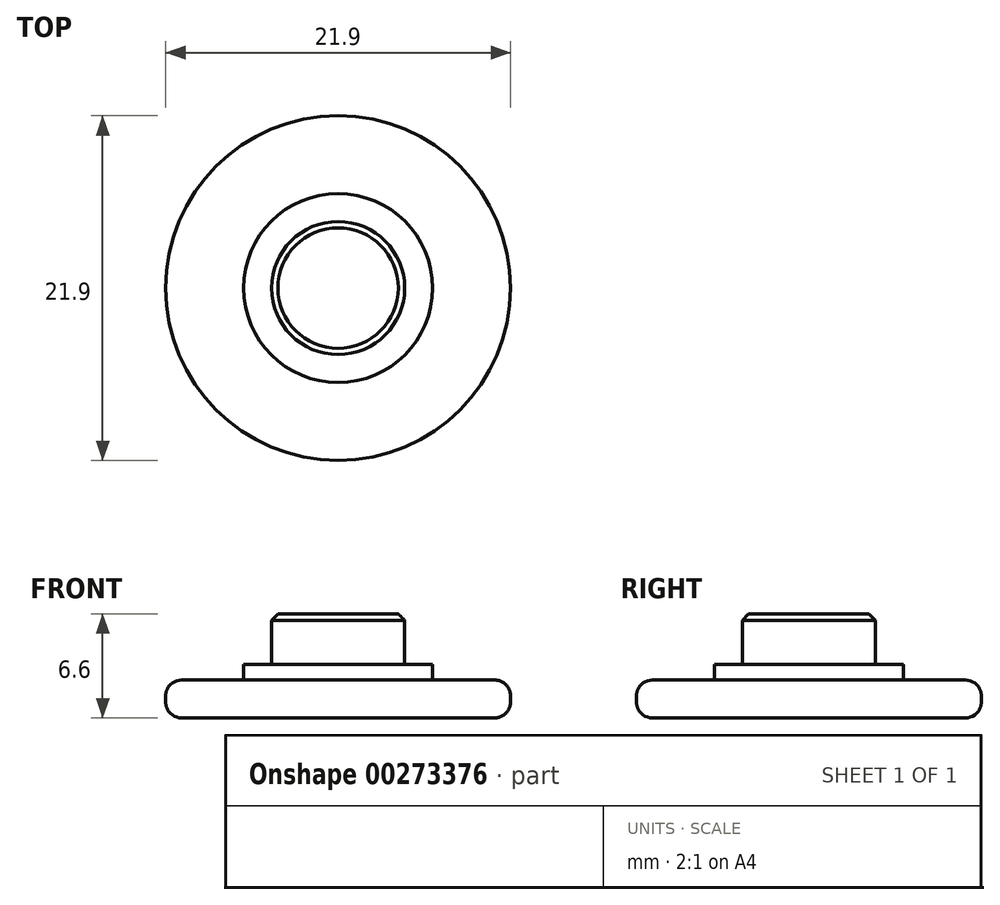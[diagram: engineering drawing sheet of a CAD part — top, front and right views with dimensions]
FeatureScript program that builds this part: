
annotation { "Feature Type Name" : "Feature", "Feature Type Description" : "" }
export const myFeature = defineFeature(function(context is Context, id is Id, definition is map)
    precondition{}
    {
        {
            var Q0;
            Q0=qCreatedBy(makeId("Top.planeOp"),FACE);
            var sketch = newSketch(context, id + "F0", { "sketchPlane" : qUnion([Q0])});
            skCircle(sketch, "E0", {"center": v(0, 0) * mm, "radius": 10.95 * mm});
            skSolve(sketch);
        }
        {
            var Q0;
            Q0=makeQuery(id+"F0.imprint","IMPRINT",FACE,{"disambiguationData":[TD([[makeQuery(id+"F0.imprint","IMPRINT",EDGE,{"derivedFrom":sQuery(id+"F0.wireOp",EDGE,"E0")}),1.0]])]});
            extrude(context, id + "F1", {"entities" : qUnion([Q0]), "depth" : 2.4 * mm});
        }
        {
            var Q0;
            Q0=makeQuery(id+"F1.opExtrude","CAP_FACE",FACE,{"disambiguationData":[OSD([sQuery(id+"F0.wireOp",EDGE,"E0")])],"isStart":false});
            var sketch = newSketch(context, id + "F2", { "sketchPlane" : qUnion([Q0])});
            skCircle(sketch, "E1", {"center": v(0, 0) * mm, "radius": 4.22 * mm});
            skSolve(sketch);
        }
        {
            var Q0;
            Q0=makeQuery(id+"F2.imprint","IMPRINT",FACE,{"disambiguationData":[TD([[makeQuery(id+"F2.imprint","IMPRINT",EDGE,{"derivedFrom":sQuery(id+"F2.wireOp",EDGE,"E1")}),1.0]])]});
            extrude(context, id + "F3", {"entities" : qUnion([Q0]), "operationType" : NewBodyOperationType.ADD, "depth" : 4.2 * mm});
        }
        {
            var Q0;
            Q0=makeQuery(id+"F1.opExtrude","CAP_EDGE",EDGE,{"disambiguationData":[OSD([sQuery(id+"F0.wireOp",EDGE,"E0")])],"isStart":false});
            fillet(context, id + "F4", {"entities" : qUnion([Q0]), "radius" : 1 * mm, "tangentPropagation" : true, "allowEdgeOverflow" : false});
        }
        {
            var Q0;
            Q0=makeQuery(id+"F1.opExtrude","CAP_FACE",FACE,{"disambiguationData":[OSD([sQuery(id+"F0.wireOp",EDGE,"E0")])],"isStart":false});
            var sketch = newSketch(context, id + "F5", { "sketchPlane" : qUnion([Q0])});
            skCircle(sketch, "E2", {"center": v(0, 0) * mm, "radius": 6 * mm});
            skSolve(sketch);
        }
        {
            var Q0;
            Q0=makeQuery(id+"F5.imprint","IMPRINT",FACE,{"disambiguationData":[TD([[makeQuery(id+"F5.imprint","IMPRINT",EDGE,{"derivedFrom":sQuery(id+"F5.wireOp",EDGE,"E2")}),1.0]])]});
            extrude(context, id + "F6", {"entities" : qUnion([Q0]), "operationType" : NewBodyOperationType.ADD, "depth" : 1 * mm});
        }
        {
            var Q0;
            Q0=makeQuery(id+"F1.opExtrude","CAP_EDGE",EDGE,{"disambiguationData":[OSD([sQuery(id+"F0.wireOp",EDGE,"E0")])],"isStart":true});
            fillet(context, id + "F7", {"entities" : qUnion([Q0]), "radius" : 1 * mm, "tangentPropagation" : true, "allowEdgeOverflow" : false});
        }
        {
            var Q0;
            Q0=makeQuery(id+"F3.opExtrude","CAP_EDGE",EDGE,{"disambiguationData":[OSD([sQuery(id+"F2.wireOp",EDGE,"E1")])],"isStart":false});
            chamfer(context, id + "F8", {"entities" : qUnion([Q0]), "width" : .4 * mm, "tangentPropagation" : true});
        }
    });
